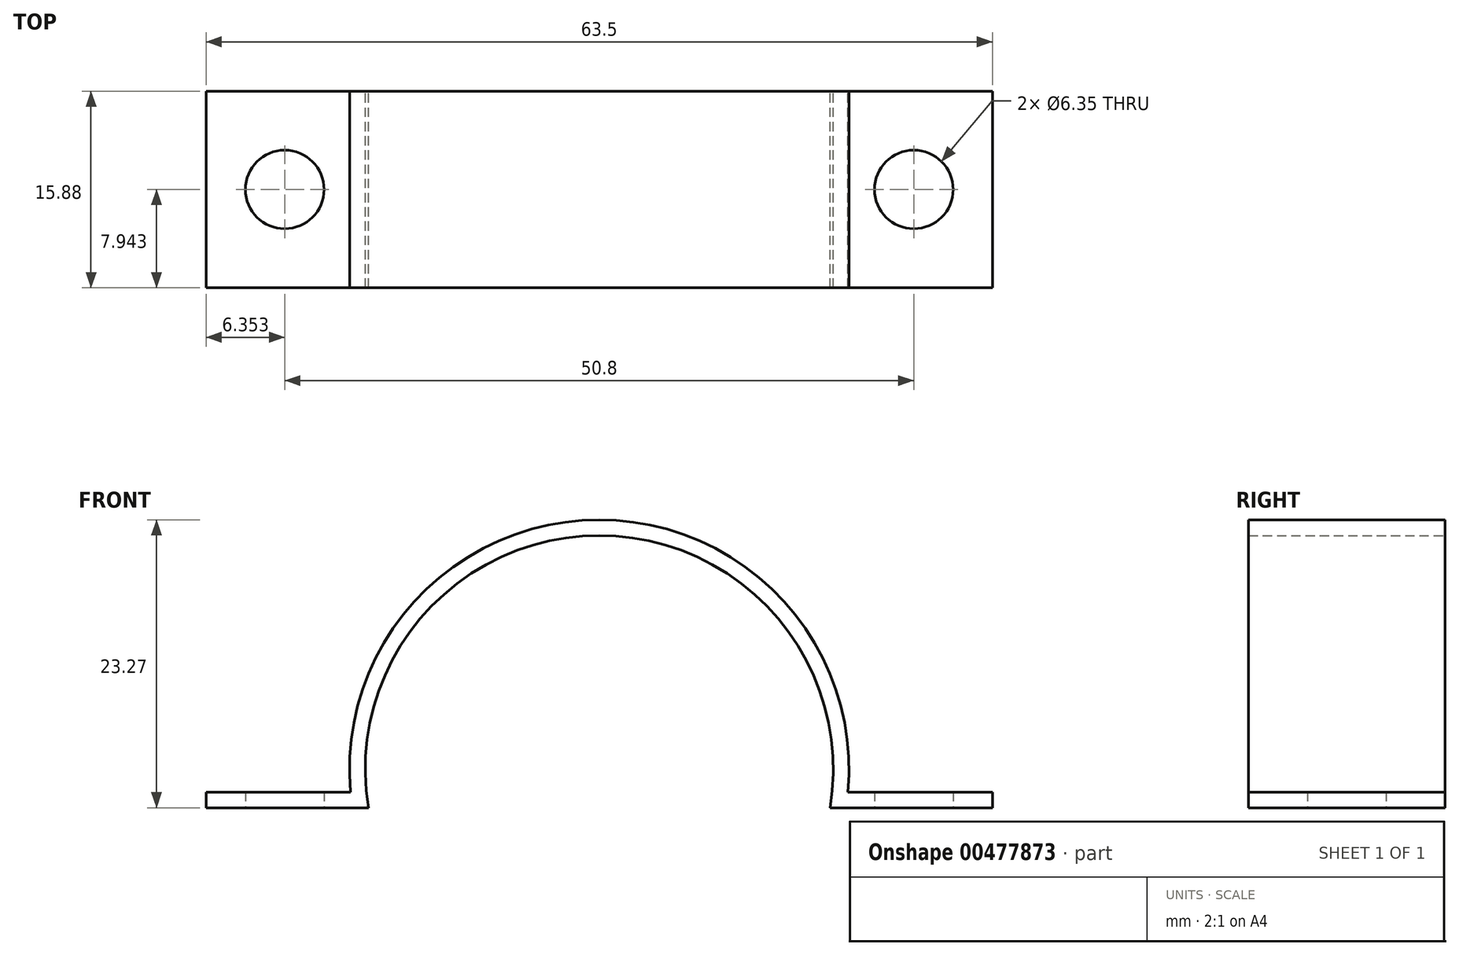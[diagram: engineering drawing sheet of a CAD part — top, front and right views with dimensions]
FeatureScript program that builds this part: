
annotation { "Feature Type Name" : "Feature", "Feature Type Description" : "" }
export const myFeature = defineFeature(function(context is Context, id is Id, definition is map)
    precondition{}
    {
        {
            var Q0;
            Q0=qCreatedBy(makeId("Front.planeOp"),FACE);
            var sketch = newSketch(context, id + "F0", { "sketchPlane" : qUnion([Q0])});
            skLineSegment(sketch, "E0", {"start": v(-26.84, -18.42) * mm, "end": v(-39.95, -18.42) * mm});
            skLineSegment(sketch, "E1", {"start": v(-39.95, -18.42) * mm, "end": v(-39.95, -17.15) * mm});
            skLineSegment(sketch, "E2", {"start": v(-39.95, -17.15) * mm, "end": v(-28.28, -17.15) * mm});
            skArc(sketch, "E3", {"start": v(11.89, -17.15) * mm, "mid": v(-8.2, 4.85) * mm, "end": v(-28.28, -17.15) * mm});
            skLineSegment(sketch, "E4", {"start": v(11.89, -17.15) * mm, "end": v(23.55, -17.15) * mm});
            skLineSegment(sketch, "E5", {"start": v(23.55, -17.15) * mm, "end": v(23.55, -18.42) * mm});
            skLineSegment(sketch, "E6", {"start": v(23.55, -18.42) * mm, "end": v(10.44, -18.42) * mm});
            skArc(sketch, "E7", {"start": v(10.44, -18.42) * mm, "mid": v(-8.2, 3.58) * mm, "end": v(-26.84, -18.42) * mm});
            skLineSegment(sketch, "E8", {"start": v(-8.2, 3.58) * mm, "end": v(-8.2, 4.85) * mm, "construction": true});
            skLineSegment(sketch, "E9", {"start": v(10.44, -18.42) * mm, "end": v(-26.84, -18.42) * mm, "construction": true});
            skLineSegment(sketch, "E10", {"start": v(-8.2, -18.42) * mm, "end": v(-8.2, 3.58) * mm, "construction": true});
            skSolve(sketch);
        }
        {
            var Q0;
            Q0=makeQuery(id+"F0.imprint","IMPRINT",FACE,{"disambiguationData":[TD([[makeQuery(id+"F0.imprint","IMPRINT",EDGE,{"derivedFrom":sQuery(id+"F0.wireOp",EDGE,"E0")}),-1.0]])]});
            extrude(context, id + "F1", {"entities" : qUnion([Q0]), "depth" : 15.88 * mm, "offsetDistance" : 25.4 * mm});
        }
        {
            var Q0;
            Q0=makeQuery(id+"F1.opExtrude","SWEPT_FACE",FACE,{"disambiguationData":[OSD([sQuery(id+"F0.wireOp",EDGE,"E0")])]});
            var sketch = newSketch(context, id + "F2", { "sketchPlane" : qUnion([Q0])});
            skPoint(sketch, "E11.0", {"position": v(-39.95, 7.94) * mm});
            skPoint(sketch, "E12.0", {"position": v(23.55, 7.94) * mm});
            skPoint(sketch, "E13.endSnap0", {"position": v(-26.84, 7.94) * mm});
            skLineSegment(sketch, "E14", {"start": v(17.2, 7.94) * mm, "end": v(23.55, 7.94) * mm, "construction": true});
            skLineSegment(sketch, "E15", {"start": v(17.2, 7.94) * mm, "end": v(-33.6, 7.94) * mm, "construction": true});
            skLineSegment(sketch, "E16", {"start": v(-33.6, 7.94) * mm, "end": v(-39.95, 7.94) * mm, "construction": true});
            skSolve(sketch);
        }
        {
            var Q0;
            Q0=sQuery(id+"F2.wireOp",VERTEX,"E16.start");
            var Q1;
            Q1=sQuery(id+"F2.wireOp",VERTEX,"E15.start");
            var Q2;
            Q2=makeQuery(id+"F1.opExtrude","SWEPT_BODY",BODY,{"disambiguationData":[OSD([sQuery(id+"F0.wireOp",EDGE,"E0"),sQuery(id+"F0.wireOp",EDGE,"E1"),sQuery(id+"F0.wireOp",EDGE,"E2"),sQuery(id+"F0.wireOp",EDGE,"E3"),sQuery(id+"F0.wireOp",EDGE,"E4"),sQuery(id+"F0.wireOp",EDGE,"E5"),sQuery(id+"F0.wireOp",EDGE,"E6"),sQuery(id+"F0.wireOp",EDGE,"E7")])]});
            hole(context, id + "F3", {"style" : HoleStyle.SIMPLE, "endStyle" : HoleEndStyle.THROUGH, "holeDiameter" : 6.35 * mm, "isTappedThrough" : true, "tappedDepth" : 12.7 * mm, "tapClearance" : 3, "locations" : qUnion([Q0, Q1]), "scope" : qUnion([Q2])});
        }
    });
